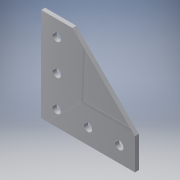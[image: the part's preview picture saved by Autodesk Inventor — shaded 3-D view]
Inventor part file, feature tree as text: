
AUTODESK INVENTOR PART (.ipt)
format: ipt  version: 2016 (Build 200138000, 138)  size: 104,448 bytes
history: native  units: in
note: dims shown in document units (in); Inventor stores cm internally (conversion verified against a paired STEP export)
features: other x3, sketch x1
ambient origin geometry x8: Origin, YZ Plane, XZ Plane, XY Plane, X Axis, Y Axis, Z Axis, Center Point
bodies: Solid1 (feature_tree)
feature tree (4):
  other  "gusset plate.ipt"
  other  "Solid1::gusset plate.ipt"
  other  "TaggingFeature1"
  sketch  "Sketch1"  dims[d0=0.3937in]
